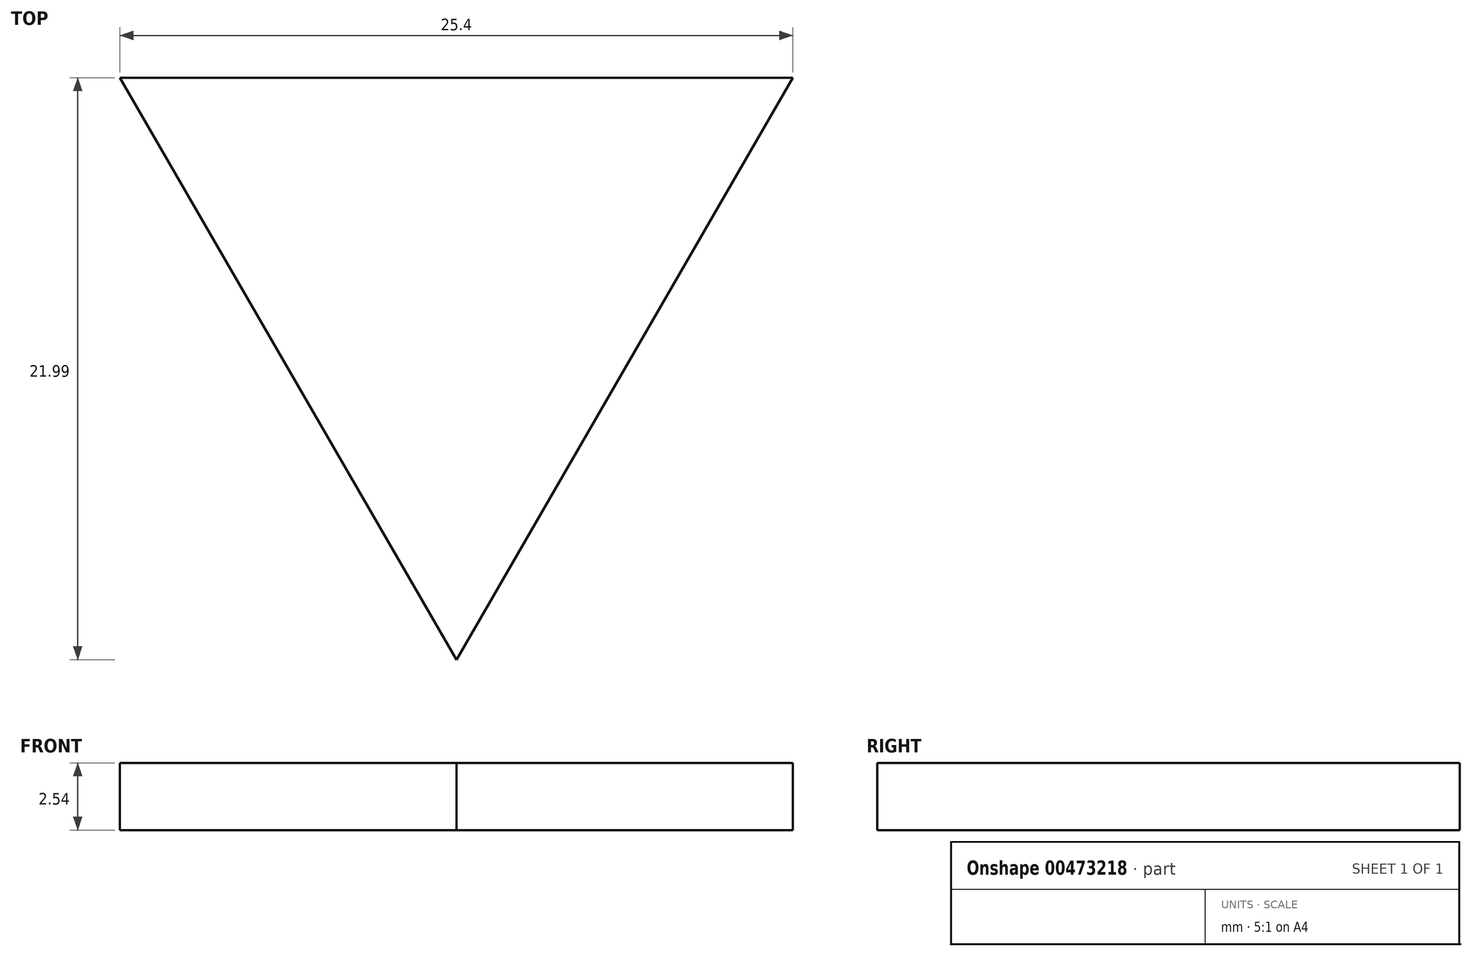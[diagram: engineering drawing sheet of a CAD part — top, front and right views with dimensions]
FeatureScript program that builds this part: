
annotation { "Feature Type Name" : "Feature", "Feature Type Description" : "" }
export const myFeature = defineFeature(function(context is Context, id is Id, definition is map)
    precondition{}
    {
        {
            var Q0;
            Q0=qCreatedBy(makeId("Top.planeOp"),FACE);
            var sketch = newSketch(context, id + "F0", { "sketchPlane" : qUnion([Q0])});
            skCircle(sketch, "E0", {"center": v(0, 0) * mm, "radius": 5.65 * mm});
            skCircle(sketch, "E1.cCircle", {"center": v(0, 0) * mm, "radius": 7.33 * mm, "construction": true});
            skLineSegment(sketch, "E1.0", {"start": v(-12.7, 7.33) * mm, "end": v(12.7, 7.33) * mm});
            skLineSegment(sketch, "E1.1", {"start": v(12.7, 7.33) * mm, "end": v(0, -14.66) * mm});
            skLineSegment(sketch, "E1.2", {"start": v(0, -14.66) * mm, "end": v(-12.7, 7.33) * mm});
            skPoint(sketch, "E1.0.midPoint", {"position": v(0, 7.33) * mm});
            skSolve(sketch);
        }
        {
            var Q0;
            Q0=makeQuery(id+"F0.imprint","IMPRINT",FACE,{"disambiguationData":[TD([[makeQuery(id+"F0.imprint","IMPRINT",EDGE,{"derivedFrom":sQuery(id+"F0.wireOp",EDGE,"E0")}),-1.0]])]});
            var Q1;
            Q1=makeQuery(id+"F0.imprint","IMPRINT",FACE,{"disambiguationData":[TD([[makeQuery(id+"F0.imprint","IMPRINT",EDGE,{"derivedFrom":sQuery(id+"F0.wireOp",EDGE,"E0")}),1.0]])]});
            extrude(context, id + "F1", {"entities" : qUnion([Q0, Q1]), "depth" : 2.54 * mm});
        }
    });
